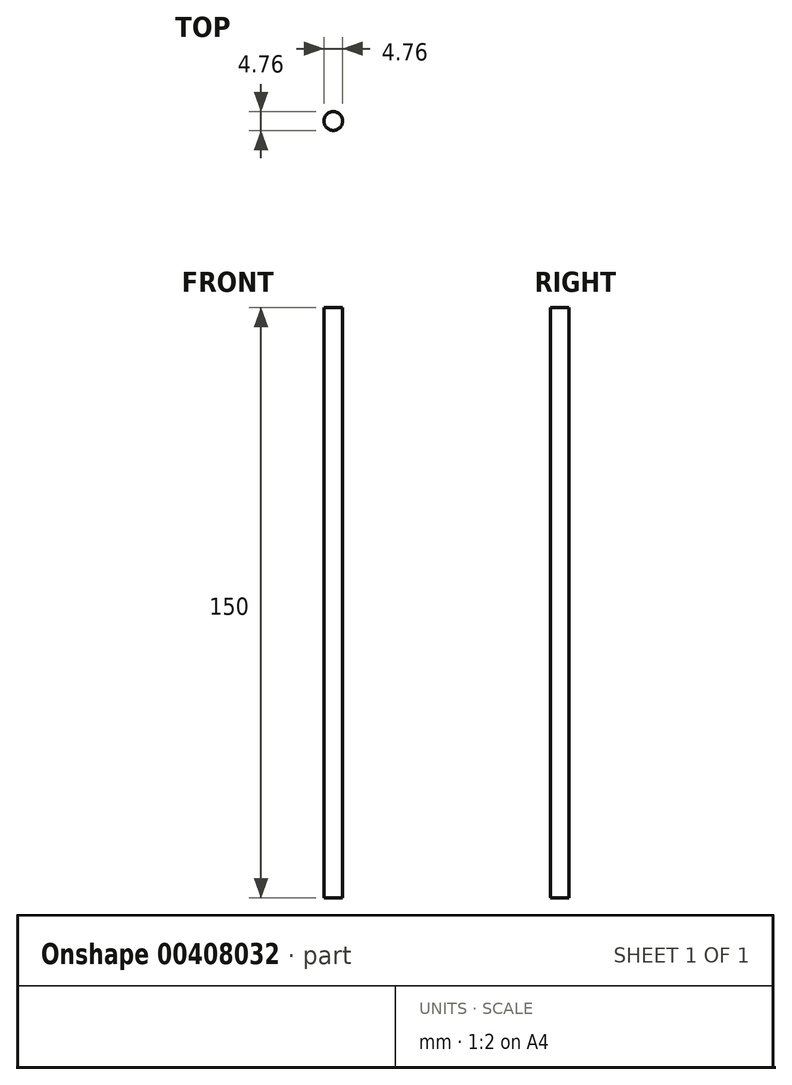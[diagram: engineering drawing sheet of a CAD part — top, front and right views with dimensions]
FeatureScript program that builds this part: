
annotation { "Feature Type Name" : "Feature", "Feature Type Description" : "" }
export const myFeature = defineFeature(function(context is Context, id is Id, definition is map)
    precondition{}
    {
        {
            var Q0;
            Q0=qCreatedBy(makeId("Top.planeOp"),FACE);
            var sketch = newSketch(context, id + "F0", { "sketchPlane" : qUnion([Q0])});
            skCircle(sketch, "E0", {"center": v(0, 0) * mm, "radius": 2.38 * mm});
            skSolve(sketch);
        }
        {
            var Q0;
            Q0=makeQuery(id+"F0.imprint","IMPRINT",FACE,{"disambiguationData":[TD([[makeQuery(id+"F0.imprint","IMPRINT",EDGE,{"derivedFrom":sQuery(id+"F0.wireOp",EDGE,"E0")}),1.0]])]});
            extrude(context, id + "F1", {"entities" : qUnion([Q0]), "endBound" : BoundingType.SYMMETRIC, "depth" : 150 * mm, "offsetDistance" : 25.4 * mm});
        }
    });
